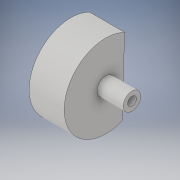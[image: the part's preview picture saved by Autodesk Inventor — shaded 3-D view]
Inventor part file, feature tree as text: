
AUTODESK INVENTOR PART (.ipt)
format: ipt  version: 2019 (Build 230136000, 136)  size: 129,024 bytes
history: native  units: in
note: dims shown in document units (in); Inventor stores cm internally (conversion verified against a paired STEP export)
features: extrude x5, sketch x5, projected_geometry x1
ambient origin geometry x8: Origin, YZ Plane, XZ Plane, XY Plane, X Axis, Y Axis, Z Axis, Center Point
bodies: Solid1 (feature_tree)
feature tree (11):
  extrude  "Extrusion1"  Depth=2.375in
  extrude  "Extrusion2"  Depth=0.25in TaperAngle=0.0deg
  extrude  "Extrusion3"  Depth=0.25in TaperAngle=0.0deg
  extrude  "Extrusion4"  Depth=0.25in TaperAngle=0.0deg
  extrude  "Extrusion5"  Depth=0.75in
  sketch  "Sketch1"  dims[d0=2.25in d1=2.375in]
  sketch  "Sketch2"  dims[d2=1.0in d3=0.0in d4=0.25in d5=0.0in]
  projected_geometry  "Projected Loop1"
  sketch  "Sketch3"  dims[d6=2.15in d7=0.25in d8=0.0in]
  sketch  "Sketch4"  dims[d9=0.25in d10=0.25in d11=0.0in]
  sketch  "Sketch5"  dims[d12=0.25in d13=0.5in d14=0.75in d15=0.0in]
